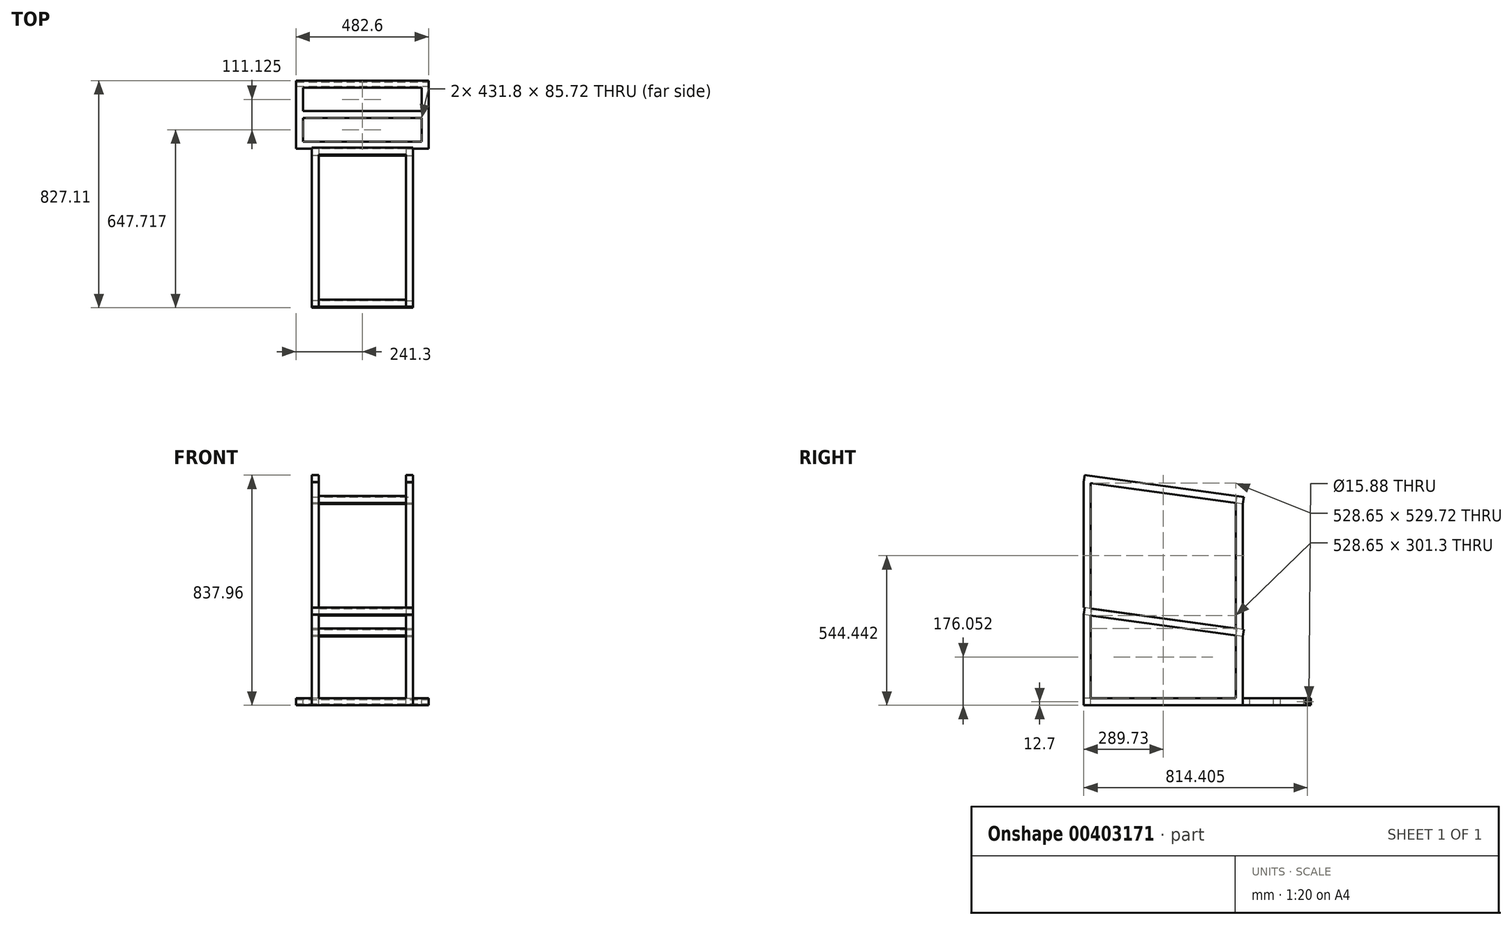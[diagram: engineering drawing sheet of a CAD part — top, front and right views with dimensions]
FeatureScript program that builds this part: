
annotation { "Feature Type Name" : "Feature", "Feature Type Description" : "" }
export const myFeature = defineFeature(function(context is Context, id is Id, definition is map)
    precondition{}
    {
        {
            var Q0;
            Q0=qCreatedBy(makeId("Top.planeOp"),FACE);
            var sketch = newSketch(context, id + "F0", { "sketchPlane" : qUnion([Q0])});
            skLineSegment(sketch, "E0.bottom", {"start": v(215.9, 98.43) * mm, "end": v(-215.9, 98.43) * mm});
            skLineSegment(sketch, "E0.top", {"start": v(215.9, -98.43) * mm, "end": v(-215.9, -98.43) * mm});
            skLineSegment(sketch, "E0.left", {"start": v(215.9, 98.43) * mm, "end": v(215.9, -98.42) * mm});
            skLineSegment(sketch, "E0.right", {"start": v(-215.9, 98.43) * mm, "end": v(-215.9, -98.42) * mm});
            skPoint(sketch, "E0.middle", {"position": v(0, 0) * mm});
            skLineSegment(sketch, "E1.0", {"start": v(-241.3, 123.83) * mm, "end": v(-241.3, -123.82) * mm});
            skLineSegment(sketch, "E1.1", {"start": v(241.3, 123.83) * mm, "end": v(-241.3, 123.83) * mm});
            skLineSegment(sketch, "E1.2", {"start": v(241.3, 123.83) * mm, "end": v(241.3, -123.82) * mm});
            skLineSegment(sketch, "E1.3", {"start": v(241.3, -123.83) * mm, "end": v(-241.3, -123.83) * mm});
            skLineSegment(sketch, "E2.top", {"start": v(158.75, -677.88) * mm, "end": v(-158.75, -677.88) * mm});
            skLineSegment(sketch, "E2.left", {"start": v(158.75, -123.83) * mm, "end": v(158.75, -677.88) * mm});
            skLineSegment(sketch, "E2.right", {"start": v(-158.75, -123.83) * mm, "end": v(-158.75, -677.88) * mm});
            skPoint(sketch, "E2.middle", {"position": v(0, -400.85) * mm});
            skLineSegment(sketch, "E3.0", {"start": v(184.15, -123.83) * mm, "end": v(184.15, -703.28) * mm});
            skLineSegment(sketch, "E3.1", {"start": v(184.15, -703.28) * mm, "end": v(-184.15, -703.28) * mm});
            skLineSegment(sketch, "E3.2", {"start": v(-184.15, -123.83) * mm, "end": v(-184.15, -703.28) * mm});
            skLineSegment(sketch, "E4.bottom", {"start": v(215.9, 12.7) * mm, "end": v(-215.9, 12.7) * mm});
            skLineSegment(sketch, "E4.top", {"start": v(215.9, -12.7) * mm, "end": v(-215.9, -12.7) * mm});
            skLineSegment(sketch, "E4.left", {"start": v(215.9, 12.7) * mm, "end": v(215.9, -12.7) * mm});
            skLineSegment(sketch, "E4.right", {"start": v(-215.9, 12.7) * mm, "end": v(-215.9, -12.7) * mm});
            skSolve(sketch);
        }
        {
            var Q0;
            Q0=makeQuery(id+"F0.imprint","IMPRINT",FACE,{"disambiguationData":[TD([[makeQuery(id+"F0.imprint","IMPRINT",EDGE,{"derivedFrom":sQuery(id+"F0.wireOp",EDGE,"E4.bottom")}),1.0]])]});
            var Q1;
            Q1=makeQuery(id+"F0.imprint","IMPRINT",FACE,{"disambiguationData":[TD([[makeQuery(id+"F0.imprint","IMPRINT",EDGE,{"derivedFrom":sQuery(id+"F0.wireOp",EDGE,"E2.top")}),1.0]])]});
            var Q2;
            {var subQ8=sQuery(id+"F0.wireOp",EDGE,"E0.bottom");Q2=makeQuery(id+"F0.imprint","IMPRINT",FACE,{"disambiguationData":[TD([[makeQuery(id+"F0.imprint","IMPRINT",EDGE,{"derivedFrom":subQ8}),-1.0]])]});}
            extrude(context, id + "F1", {"entities" : qUnion([Q0, Q1, Q2]), "oppositeDirection" : true, "depth" : 25.4 * mm});
        }
        {
            var Q0;
            Q0=makeQuery(id+"F1.opExtrude","SWEPT_FACE",FACE,{"disambiguationData":[OSD([sQuery(id+"F0.wireOp",EDGE,"E3.0")])]});
            var sketch = newSketch(context, id + "F2", { "sketchPlane" : qUnion([Q0])});
            skLineSegment(sketch, "E5", {"start": v(-703.28, 0) * mm, "end": v(-703.28, 304.8) * mm});
            skLineSegment(sketch, "E6", {"start": v(-703.28, 304.8) * mm, "end": v(-123.83, 225.04) * mm});
            skLineSegment(sketch, "E7", {"start": v(-123.83, 0) * mm, "end": v(-123.83, 225.04) * mm});
            skLineSegment(sketch, "E8", {"start": v(-677.88, 0) * mm, "end": v(-677.88, 301.3) * mm});
            skLineSegment(sketch, "E9.0", {"start": v(-149.22, 0) * mm, "end": v(-149.22, 228.54) * mm});
            skLineSegment(sketch, "E10.0", {"start": v(-699.81, 329.96) * mm, "end": v(-120.36, 250.2) * mm});
            skLineSegment(sketch, "E11", {"start": v(-703.28, 304.8) * mm, "end": v(-699.81, 329.96) * mm});
            skLineSegment(sketch, "E12", {"start": v(-120.36, 250.2) * mm, "end": v(-123.83, 225.04) * mm});
            skLineSegment(sketch, "E13", {"start": v(-703.28, 330.44) * mm, "end": v(-703.28, 787.4) * mm});
            skLineSegment(sketch, "E14.0", {"start": v(-677.88, 326.94) * mm, "end": v(-677.88, 783.9) * mm});
            skLineSegment(sketch, "E15", {"start": v(-703.28, 330.44) * mm, "end": v(-677.88, 326.94) * mm});
            skLineSegment(sketch, "E16", {"start": v(-703.28, 787.4) * mm, "end": v(-123.82, 707.64) * mm});
            skLineSegment(sketch, "E17", {"start": v(-149.22, 254.18) * mm, "end": v(-149.22, 711.14) * mm});
            skLineSegment(sketch, "E18", {"start": v(-703.28, 787.4) * mm, "end": v(-677.88, 783.9) * mm});
            skLineSegment(sketch, "E19.0", {"start": v(-699.81, 812.56) * mm, "end": v(-120.36, 732.8) * mm});
            skLineSegment(sketch, "E20", {"start": v(-699.81, 812.56) * mm, "end": v(-703.28, 787.4) * mm});
            skLineSegment(sketch, "E21", {"start": v(-120.36, 732.8) * mm, "end": v(-123.82, 707.64) * mm});
            skLineSegment(sketch, "E22", {"start": v(-677.88, 301.3) * mm, "end": v(-674.41, 326.47) * mm});
            skLineSegment(sketch, "E23", {"start": v(-149.23, 228.54) * mm, "end": v(-145.76, 253.7) * mm});
            skLineSegment(sketch, "E24", {"start": v(-149.22, 711.14) * mm, "end": v(-145.76, 736.3) * mm});
            skLineSegment(sketch, "E25", {"start": v(-677.88, 783.9) * mm, "end": v(-674.41, 809.07) * mm});
            skLineSegment(sketch, "E26", {"start": v(-149.23, 228.54) * mm, "end": v(-149.22, 254.18) * mm, "construction": true});
            skLineSegment(sketch, "E27", {"start": v(-123.82, 250.68) * mm, "end": v(-123.82, 707.64) * mm});
            skLineSegment(sketch, "E28", {"start": v(-123.83, 225.04) * mm, "end": v(-123.82, 250.68) * mm, "construction": true});
            skSolve(sketch);
        }
        {
            var Q0;
            Q0 = qSketchRegion(id + "F2", true);
            var Q1;
            {var subQ0=sQuery(id+"F2.wireOp",EDGE,"E5");Q1=makeQuery(id+"F2.imprint","IMPRINT",FACE,{"disambiguationData":[TD([[makeQuery(id+"F2.imprint","IMPRINT",EDGE,{"derivedFrom":subQ0}),-1.0]])]});}
            var Q2;
            {var subQ0=sQuery(id+"F2.wireOp",EDGE,"E7");Q2=makeQuery(id+"F2.imprint","IMPRINT",FACE,{"disambiguationData":[TD([[makeQuery(id+"F2.imprint","IMPRINT",EDGE,{"derivedFrom":subQ0}),1.0]])]});}
            extrude(context, id + "F3", {"entities" : qUnion([Q0, Q1, Q2]), "oppositeDirection" : true, "depth" : 25.4 * mm});
        }
        {
            var Q0;
            Q0=makeQuery(id+"F3.opExtrude","SWEPT_BODY",BODY,{"disambiguationData":[OSD([sQuery(id+"F0.wireOp",EDGE,"E3.0"),sQuery(id+"F2.wireOp",EDGE,"E5"),sQuery(id+"F2.wireOp",EDGE,"E6"),sQuery(id+"F2.wireOp",EDGE,"E7"),sQuery(id+"F2.wireOp",EDGE,"E8"),sQuery(id+"F2.wireOp",EDGE,"E9.0"),sQuery(id+"F2.wireOp",EDGE,"E10.0"),sQuery(id+"F2.wireOp",EDGE,"E11"),sQuery(id+"F2.wireOp",EDGE,"E12"),sQuery(id+"F2.wireOp",EDGE,"E13"),sQuery(id+"F2.wireOp",EDGE,"E14.0"),sQuery(id+"F2.wireOp",EDGE,"E15"),sQuery(id+"F2.wireOp",EDGE,"E16"),sQuery(id+"F2.wireOp",EDGE,"E17"),sQuery(id+"F2.wireOp",EDGE,"gZdr27mr-Bntv-1hmm-ENMd-UxipAMHiC3Bz"),sQuery(id+"F2.wireOp",EDGE,"E19.0"),sQuery(id+"F2.wireOp",EDGE,"E20"),sQuery(id+"F2.wireOp",EDGE,"E21")])]});
            var Q1;
            Q1=qCreatedBy(makeId("Right.planeOp"),FACE);
            mirror(context, id + "F4", {"operationType" : NewBodyOperationType.ADD, "entities" : qUnion([Q0]), "mirrorPlane" : qUnion([Q1])});
        }
        {
            var Q0;
            {var subQ3=sQuery(id+"F2.wireOp",EDGE,"E11");Q0=makeQuery(id+"F2.imprint","IMPRINT",FACE,{"disambiguationData":[TD([[makeQuery(id+"F2.imprint","IMPRINT",EDGE,{"derivedFrom":subQ3}),-1.0]])]});}
            var Q1;
            {var subQ0=sQuery(id+"F2.wireOp",EDGE,"E12");Q1=makeQuery(id+"F2.imprint","IMPRINT",FACE,{"disambiguationData":[TD([[makeQuery(id+"F2.imprint","IMPRINT",EDGE,{"derivedFrom":subQ0}),-1.0]])]});}
            var Q2;
            Q2=makeQuery(id+"F2.imprint","IMPRINT",FACE,{"disambiguationData":[TD([[makeQuery(id+"F2.imprint","IMPRINT",EDGE,{"derivedFrom":sQuery(id+"F2.wireOp",EDGE,"E18")}),1.0]])]});
            var Q3;
            {var subQ0=sQuery(id+"F2.wireOp",EDGE,"E21");Q3=makeQuery(id+"F2.imprint","IMPRINT",FACE,{"disambiguationData":[TD([[makeQuery(id+"F2.imprint","IMPRINT",EDGE,{"derivedFrom":subQ0}),-1.0]])]});}
            extrude(context, id + "F5", {"entities" : qUnion([Q0, Q1, Q2, Q3]), "operationType" : NewBodyOperationType.ADD, "oppositeDirection" : true, "depth" : 368.3 * mm});
        }
        {
            var Q0;
            Q0=makeQuery(id+"F1.opExtrude","SWEPT_FACE",FACE,{"disambiguationData":[OSD([sQuery(id+"F0.wireOp",EDGE,"E1.2")])]});
            var sketch = newSketch(context, id + "F6", { "sketchPlane" : qUnion([Q0])});
            skLineSegment(sketch, "E29", {"start": v(98.43, 0) * mm, "end": v(98.43, -25.4) * mm, "construction": true});
            skLineSegment(sketch, "E30", {"start": v(98.43, -12.7) * mm, "end": v(123.83, -12.7) * mm, "construction": true});
            skPoint(sketch, "E31", {"position": v(111.13, -12.7) * mm});
            skCircle(sketch, "E32", {"center": v(111.13, -12.7) * mm, "radius": 7.94 * mm});
            skSolve(sketch);
        }
        {
            var Q0;
            Q0=makeQuery(id+"F6.imprint","IMPRINT",FACE,{"disambiguationData":[TD([[makeQuery(id+"F6.imprint","IMPRINT",EDGE,{"derivedFrom":sQuery(id+"F6.wireOp",EDGE,"E32")}),1.0]])]});
            extrude(context, id + "F7", {"entities" : qUnion([Q0]), "operationType" : NewBodyOperationType.REMOVE, "oppositeDirection" : true, "depth" : 482.6 * mm});
        }
    });
